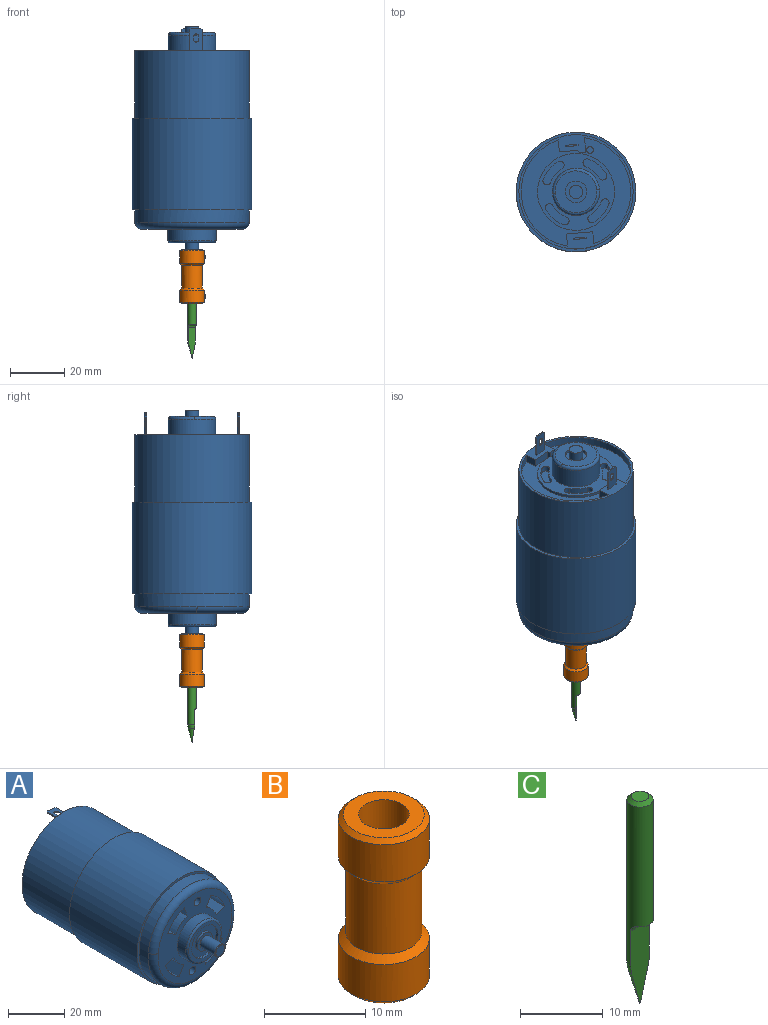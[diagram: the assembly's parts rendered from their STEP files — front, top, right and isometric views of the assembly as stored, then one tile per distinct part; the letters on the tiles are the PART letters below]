
ASSEMBLY  parts=3 mates=2
PART A: 110 faces, bbox 45.6x88x45.6 mm
  f0: torus R=18.65mm, axis (0,1,0), area 249.7mm2, adj f6,f28,f41
  f1: torus R=8.15mm, axis (0,1,0), area 31.9mm2, adj f8,f79,f85
  f2: torus R=7.75mm, axis (0,-1,0), area 41.4mm2, adj f19,f102,f104
  f3: torus R=2.25mm, axis (0,1,0), area 3mm2, adj f23,f107,f109
  f4: cylinder r=22.15mm len=44.3mm, axis (0,1,0), area 4731.9mm2, adj f25,f26
  f5: cylinder r=21.15mm len=42.3mm, axis (0,-1,0), area 3322.2mm2, adj f25,f27
  f6: cylinder r=21.15mm len=42.3mm, axis (0,-1,0), area 611.3mm2, adj f0,f26,f28
  f7: cylinder r=20.3mm len=39.26mm, axis (0,1,0), area 151mm2, adj f27,f31,f38,f51
  f8: cylinder r=8.9mm len=17.8mm, axis (0,-1,0), area 237.7mm2, adj f1,f41,f79
  f9: cylinder r=1.65mm len=11.5mm, axis (0,-1,0), area 119.2mm2, adj f13,f41
  f10: cylinder r=1.65mm len=11.5mm, axis (0,-1,0), area 119.2mm2, adj f14,f41
  f11: cylinder r=14.25mm len=28.5mm, axis (0,1,0), area 89.5mm2, adj f51,f83
  f12: cylinder r=1.25mm len=2.5mm, axis (0,1,0), area 0.8mm2, adj f51,f84
  f13: cone r=1.65mm half-angle=59deg, axis (0,-1,0), area 10mm2, adj f9
  f14: cone r=1.65mm half-angle=59deg, axis (0,-1,0), area 10mm2, adj f10
  f15: cylinder r=1.5mm len=2.9mm, axis (0,1,0), area 9.4mm2, adj f83,f86,f87,f98
  f16: cylinder r=1.5mm len=2.9mm, axis (0,1,0), area 9.4mm2, adj f83,f89,f90,f99
  f17: cylinder r=1.5mm len=2.79mm, axis (0,1,0), area 9.4mm2, adj f83,f92,f94,f100
  f18: cylinder r=1.5mm len=2.79mm, axis (0,1,0), area 9.4mm2, adj f83,f95,f97,f101
  f19: cylinder r=8.75mm len=17.5mm, axis (0,-1,0), area 412.3mm2, adj f2,f83,f102
  f20: cylinder r=6.62mm len=13.25mm, axis (0,-1,0), area 41.6mm2, adj f85,f103
  f21: cylinder r=3.75mm len=7.5mm, axis (0,-1,0), area 23.6mm2, adj f103,f105
  f22: cylinder r=4mm len=8mm, axis (0,1,0), area 25.1mm2, adj f104,f106
  f23: cylinder r=2.5mm len=7.55mm, axis (0,-1,0), area 118.6mm2, adj f3,f105,f107
  f24: cylinder r=2.5mm len=5mm, axis (0,-1,0), area 53.4mm2, adj f106,f108
  f25: plane 44.3x44.3mm, normal (0,1,0), area 136mm2, adj f4,f5
  f26: plane 44.3x44.3mm, normal (0,-1,0), area 136mm2, adj f4,f6
  f27: plane 42.3x42.3mm, normal (0,1,0), area 203.5mm2, adj f5,f7,f29,f30,f31,f32,f33,f34
  f28: torus R=18.65mm, axis (0,1,0), area 249.7mm2, adj f0,f6,f41
  f29: plane 8.15x4.58mm, normal (0.09,0,1), area 32.1mm2, adj f27,f42,f43,f44,f45,f46,f47,f48
  f30: plane 8.15x4.58mm, normal (-0.09,0,-1), area 32.1mm2, adj f27,f42,f43,f44,f45,f46,f47,f48
  f31: plane 4.44x2.8mm, normal (1,0,-0.09), area 12.5mm2, adj f7,f27,f32,f51
  f32: plane 9.71x2.8mm, normal (-0.09,0,-1), area 27.3mm2, adj f27,f31,f33,f51
  f33: plane 4.44x2.8mm, normal (-1,0,0.09), area 12.5mm2, adj f27,f32,f34,f51
  f34: cylinder r=20.3mm len=39.26mm, axis (0,1,0), area 151mm2, adj f27,f33,f35,f51
  f35: plane 4.44x2.8mm, normal (-1,0,0.09), area 12.5mm2, adj f27,f34,f36,f51
  f36: plane 6.92x2.8mm, normal (0.09,0,1), area 19.4mm2, adj f27,f35,f51,f52
  f37: plane 2.8x2.8mm, normal (0.09,0,1), area 7.9mm2, adj f27,f38,f51,f52
  f38: plane 5.44x2.8mm, normal (1,0,-0.09), area 15.3mm2, adj f7,f27,f37,f51
  f39: plane 8.15x4.58mm, normal (-0.09,0,-1), area 32.1mm2, adj f27,f53,f54,f55,f56,f57,f58,f59
  f40: plane 8.15x4.58mm, normal (0.09,0,1), area 32.1mm2, adj f27,f53,f54,f55,f56,f57,f58,f59
  f41: plane 37.3x37.3mm, normal (0,-1,0), area 647.6mm2, adj f0,f8,f9,f10,f28,f62,f63,f64
  f42: plane 3.63x0.81mm, normal (0,1,0), area 1.8mm2, adj f29,f30,f43,f46
  f43: plane 0.54x0.54mm, normal (-0.7,0.71,0.06), area 0.4mm2, adj f29,f30,f42,f44
  f44: plane 7.65x0.5mm, normal (-1,0,0.09), area 3.8mm2, adj f27,f29,f30,f43
  f45: plane 7.65x0.5mm, normal (1,0,-0.09), area 3.8mm2, adj f27,f29,f30,f46
  f46: plane 0.54x0.54mm, normal (0.7,0.71,-0.06), area 0.4mm2, adj f29,f30,f42,f45
  f47: plane 1x0.5mm, normal (1,0,-0.09), area 0.5mm2, adj f29,f30,f48,f50
  f48: cylinder r=1mm len=2.04mm, axis (0.09,0,1), area 1.6mm2, adj f29,f30,f47,f49
  f49: plane 1x0.5mm, normal (-1,0,0.09), area 0.5mm2, adj f29,f30,f48,f50
  f50: cylinder r=1mm len=2.04mm, axis (0.09,0,1), area 1.6mm2, adj f29,f30,f47,f49
  f51: plane 40.6x40.11mm, normal (0,1,0), area 554.3mm2, adj f7,f11,f12,f31,f32,f33,f34,f35
  f52: plane 2.8x1mm, normal (-1,0,0.09), area 2.8mm2, adj f27,f36,f37,f51
  f53: plane 7.65x0.5mm, normal (-1,0,0.09), area 3.8mm2, adj f27,f39,f40,f54
  f54: plane 0.54x0.54mm, normal (-0.7,0.71,0.06), area 0.4mm2, adj f39,f40,f53,f55
  f55: plane 3.63x0.81mm, normal (0,1,0), area 1.8mm2, adj f39,f40,f54,f56
  f56: plane 0.54x0.54mm, normal (0.7,0.71,-0.06), area 0.4mm2, adj f39,f40,f55,f57
  f57: plane 7.65x0.5mm, normal (1,0,-0.09), area 3.8mm2, adj f27,f39,f40,f56
  f58: plane 1x0.5mm, normal (-1,0,0.09), area 0.5mm2, adj f39,f40,f59,f61
  f59: cylinder r=1mm len=2.04mm, axis (-0.09,0,-1), area 1.6mm2, adj f39,f40,f58,f60
  f60: plane 1x0.5mm, normal (1,0,-0.09), area 0.5mm2, adj f39,f40,f59,f61
  f61: cylinder r=1mm len=2.04mm, axis (-0.09,0,-1), area 1.6mm2, adj f39,f40,f58,f60
  f62: plane 10x4.42mm, normal (-0.94,0,-0.34), area 47mm2, adj f41,f63,f65,f78
  f63: cylinder r=11.3mm len=10mm, axis (0,-1,0), area 78.9mm2, adj f41,f62,f64,f78
  f64: plane 10x4.07mm, normal (0.5,0,0.87), area 47mm2, adj f41,f63,f65,f78
  f65: cylinder r=16mm len=10mm, axis (0,-1,0), area 111.7mm2, adj f41,f62,f64,f78
  f66: cylinder r=16mm len=10mm, axis (0,-1,0), area 111.7mm2, adj f41,f67,f69,f80
  f67: plane 10x4.42mm, normal (0.94,0,0.34), area 47mm2, adj f41,f66,f68,f80
  f68: cylinder r=11.3mm len=10mm, axis (0,-1,0), area 78.9mm2, adj f41,f67,f69,f80
  f69: plane 10x4.07mm, normal (-0.5,0,-0.87), area 47mm2, adj f41,f66,f68,f80
  f70: plane 10x4.42mm, normal (-0.34,0,0.94), area 47mm2, adj f41,f71,f73,f81
  f71: cylinder r=11.3mm len=10mm, axis (0,-1,0), area 78.9mm2, adj f41,f70,f72,f81
  f72: plane 10x4.07mm, normal (0.87,0,-0.5), area 47mm2, adj f41,f71,f73,f81
  f73: cylinder r=16mm len=10mm, axis (0,-1,0), area 111.7mm2, adj f41,f70,f72,f81
  f74: cylinder r=16mm len=10mm, axis (0,-1,0), area 111.7mm2, adj f41,f75,f77,f82
  f75: plane 10x4.42mm, normal (0.34,0,-0.94), area 47mm2, adj f41,f74,f76,f82
  f76: cylinder r=11.3mm len=10mm, axis (0,-1,0), area 78.9mm2, adj f41,f75,f77,f82
  f77: plane 10x4.07mm, normal (-0.87,0,0.5), area 47mm2, adj f41,f74,f76,f82
  f78: plane 9.99x9.39mm, normal (0,-1,0), area 44.8mm2, adj f62,f63,f64,f65
  f79: torus R=8.15mm, axis (0,1,0), area 31.9mm2, adj f1,f8,f85
  f80: plane 9.99x9.39mm, normal (0,-1,0), area 44.8mm2, adj f66,f67,f68,f69
  f81: plane 9.99x9.39mm, normal (0,-1,0), area 44.8mm2, adj f70,f71,f72,f73
  f82: plane 9.99x9.39mm, normal (0,-1,0), area 44.8mm2, adj f74,f75,f76,f77
  f83: plane 28.5x28.5mm, normal (0,1,0), area 276.5mm2, adj f11,f15,f16,f17,f18,f19,f86,f87
  f84: plane 2.5x2.5mm, normal (0,1,0), area 4.9mm2, adj f12
  f85: plane 16.3x16.3mm, normal (0,-1,0), area 70.8mm2, adj f1,f20,f79
  f86: cylinder r=13mm len=6.56mm, axis (0,1,0), area 17.5mm2, adj f15,f83,f88,f98
  f87: cylinder r=10mm len=5.05mm, axis (0,1,0), area 13.4mm2, adj f15,f83,f88,f98
  f88: cylinder r=1.5mm len=2.79mm, axis (0,1,0), area 9.4mm2, adj f83,f86,f87,f98
  f89: cylinder r=13mm len=6.56mm, axis (0,1,0), area 17.5mm2, adj f16,f83,f91,f99
  f90: cylinder r=10mm len=5.05mm, axis (0,1,0), area 13.4mm2, adj f16,f83,f91,f99
  f91: cylinder r=1.5mm len=2.79mm, axis (0,1,0), area 9.4mm2, adj f83,f89,f90,f99
  f92: cylinder r=13mm len=6.56mm, axis (0,1,0), area 17.5mm2, adj f17,f83,f93,f100
  f93: cylinder r=1.5mm len=2.9mm, axis (0,1,0), area 9.4mm2, adj f83,f92,f94,f100
  f94: cylinder r=10mm len=5.05mm, axis (0,1,0), area 13.4mm2, adj f17,f83,f93,f100
  f95: cylinder r=13mm len=6.56mm, axis (0,1,0), area 17.5mm2, adj f18,f83,f96,f101
  f96: cylinder r=1.5mm len=2.9mm, axis (0,1,0), area 9.4mm2, adj f83,f95,f97,f101
  f97: cylinder r=10mm len=5.05mm, axis (0,1,0), area 13.4mm2, adj f18,f83,f96,f101
  f98: plane 8.8x7.87mm, normal (0,1,0), area 30.2mm2, adj f15,f86,f87,f88
  f99: plane 8.8x7.87mm, normal (0,1,0), area 30.2mm2, adj f16,f89,f90,f91
  f100: plane 8.8x7.87mm, normal (0,1,0), area 30.2mm2, adj f17,f92,f93,f94
  f101: plane 8.8x7.87mm, normal (0,1,0), area 30.2mm2, adj f18,f95,f96,f97
  f102: torus R=7.75mm, axis (0,-1,0), area 41.4mm2, adj f2,f19,f104
  f103: plane 13.25x13.25mm, normal (0,-1,0), area 93.7mm2, adj f20,f21
  f104: plane 15.5x15.5mm, normal (0,1,0), area 138.4mm2, adj f2,f22,f102
  f105: plane 7.5x7.5mm, normal (0,-1,0), area 24.5mm2, adj f21,f23
  f106: plane 8x8mm, normal (0,1,0), area 30.6mm2, adj f22,f24
  f107: torus R=2.25mm, axis (0,1,0), area 3mm2, adj f3,f23,f109
  f108: plane 5x5mm, normal (0,1,0), area 19.6mm2, adj f24
  f109: plane 4.5x4.5mm, normal (0,-1,0), area 15.9mm2, adj f3,f107
PART B: 40 faces, bbox 9.8x9.1x20.1 mm
  f0: plane 0.24x0.12mm, normal (1,0,0), area 0mm2, adj f32,f39
  f1: plane 0.22x0.15mm, normal (1,0,0), area 0mm2, adj f33,f39
  f2: plane 0.17x0.01mm, normal (1,0,0), area 0mm2, adj f34,f39
  f3: plane 0.13x0.12mm, normal (1,0,0), area 0mm2, adj f25,f38
  f4: plane 0.17x0.05mm, normal (1,0,0), area 0mm2, adj f26,f38
  f5: plane 0.18x0.04mm, normal (1,0,0), area 0mm2, adj f27,f38
  f6: plane 0.13x0.12mm, normal (1,0,0), area 0mm2, adj f28,f38
  f7: plane 0.17x0.05mm, normal (1,0,0), area 0mm2, adj f29,f38
  f8: plane 0.19x0.01mm, normal (1,0,0), area 0mm2, adj f31,f39
  f9: plane 0.18x0.04mm, normal (1,0,0), area 0mm2, adj f24,f38
  f10: cylinder r=4.5mm len=9mm, axis (0,0,-1), area 120.1mm2, adj f18,f20,f23
  f11: cylinder r=4.5mm len=9mm, axis (0,0,-1), area 120.1mm2, adj f19,f21,f22
  f12: plane 8x8mm, normal (0,0,1), area 30.6mm2, adj f14,f21
  f13: plane 8x8mm, normal (0,0,-1), area 42.3mm2, adj f16,f20
  f14: cylinder r=2.5mm len=10mm, axis (0,0,1), area 157.1mm2, adj f12,f15
  f15: plane 5x5mm, normal (0,0,1), area 11.7mm2, adj f14,f16
  f16: cylinder r=1.59mm len=10mm, axis (0,0,-1), area 99.7mm2, adj f13,f15
  f17: cylinder r=3.75mm len=8.5mm, axis (0,0,-1), area 200.3mm2, adj f18,f19
  f18: cone r=4.5mm half-angle=45deg, axis (0,0,-1), area 27.5mm2, adj f10,f17
  f19: cone r=3.5mm half-angle=45deg, axis (0,0,1), area 27.5mm2, adj f11,f17
  f20: cone r=4.5mm half-angle=45deg, axis (0,0,1), area 18.9mm2, adj f10,f13
  f21: cone r=4mm half-angle=45deg, axis (0,0,-1), area 18.9mm2, adj f11,f12
  f22: cylinder r=1.5mm len=3mm, axis (-1,0,0), area 3.1mm2, adj f11,f39
  f23: cylinder r=1.5mm len=3mm, axis (-1,0,0), area 3.1mm2, adj f10,f38
  f24: plane 2.06x1.18mm, normal (0,0.98,-0.22), area 2.3mm2, adj f9,f25,f29,f30,f38
  f25: plane 2.06x0.91mm, normal (0,0.68,0.73), area 2.3mm2, adj f3,f24,f26,f30,f38
  f26: plane 2.06x1.16mm, normal (0,-0.3,0.96), area 2.3mm2, adj f4,f25,f27,f30,f38
  f27: plane 2.06x1.18mm, normal (0,-0.98,0.22), area 2.3mm2, adj f5,f26,f28,f30,f38
  f28: plane 2.06x0.91mm, normal (0,-0.68,-0.73), area 2.3mm2, adj f6,f27,f29,f30,f38
  f29: plane 2.06x1.16mm, normal (0,0.3,-0.96), area 2.3mm2, adj f7,f24,f28,f30,f38
  f30: plane 2.24x2.2mm, normal (1,0,0), area 3.4mm2, adj f24,f25,f26,f27,f28,f29
  f31: plane 2.06x1.21mm, normal (0,1,0.07), area 2.3mm2, adj f8,f32,f36,f37,f39
  f32: plane 2.05x1.09mm, normal (0,0.44,0.9), area 2.3mm2, adj f0,f31,f33,f37,f39
  f33: plane 2.05x1mm, normal (0,-0.56,0.83), area 2.3mm2, adj f1,f32,f34,f37,f39
  f34: plane 2.06x1.21mm, normal (0,-1,-0.07), area 2.3mm2, adj f2,f33,f35,f37,f39
  f35: plane 2x1.03mm, normal (0,-0.44,-0.9), area 2.3mm2, adj f34,f36,f37,f39
  f36: plane 2x0.95mm, normal (0,0.56,-0.83), area 2.3mm2, adj f31,f35,f37,f39
  f37: plane 2.29x2.07mm, normal (1,0,0), area 3.4mm2, adj f31,f32,f33,f34,f35,f36
  f38: torus R=1mm, axis (1,0,0), area 6.1mm2, adj f3,f4,f5,f6,f7,f9,f23,f24
  f39: torus R=1mm, axis (1,0,0), area 6.1mm2, adj f0,f1,f2,f8,f22,f31,f32,f33
PART C: 9 faces, bbox 3.2x3.2x30.6 mm
  f0: cylinder r=1.59mm len=23.84mm, axis (0,0,-1), area 207.9mm2, adj f3,f5,f6,f7,f8
  f1: cone r=1.59mm half-angle=15deg, axis (0,0,1), area 12.1mm2, adj f2,f3,f7
  f2: sphere r=0.1mm, area 0mm2, adj f1,f7
  f3: revolved ~3.18x1.59mm, area 6.3mm2, adj f0,f1,f7
  f4: plane 2.18x2.18mm, normal (0,0,1), area 3.7mm2, adj f8
  f5: cylinder r=1mm len=3.18mm, axis (1,0,0), area 4.7mm2, adj f0,f6,f7
  f6: plane 2.47x0.59mm, normal (0,0,-1), area 1mm2, adj f0,f5
  f7: plane 11.38x3.18mm, normal (0,-1,0), area 27.6mm2, adj f0,f1,f2,f3,f5
  f8: cone r=1.09mm half-angle=45deg, axis (0,0,-1), area 5.9mm2, adj f0,f4
PLACE A rot(axis=(1,0,0),90deg) t=(0,-67.07,-55.1)mm fixed
PLACE B rot(axis=(0,0,1),35.2deg) t=(-3.5,-5.98,-119.83)mm
PLACE C rot(axis=(0,0,1),35.2deg) t=(-3.5,-5.98,-134.33)mm
MATE revolute B.f10 <-> A.f102  axis (0,0,1) through (-3.5,-5.98,-104.83)mm
MATE fastened C.f1 <-> B.f10  axis (0,0,-1) through (-3.5,-5.98,-109.83)mm
